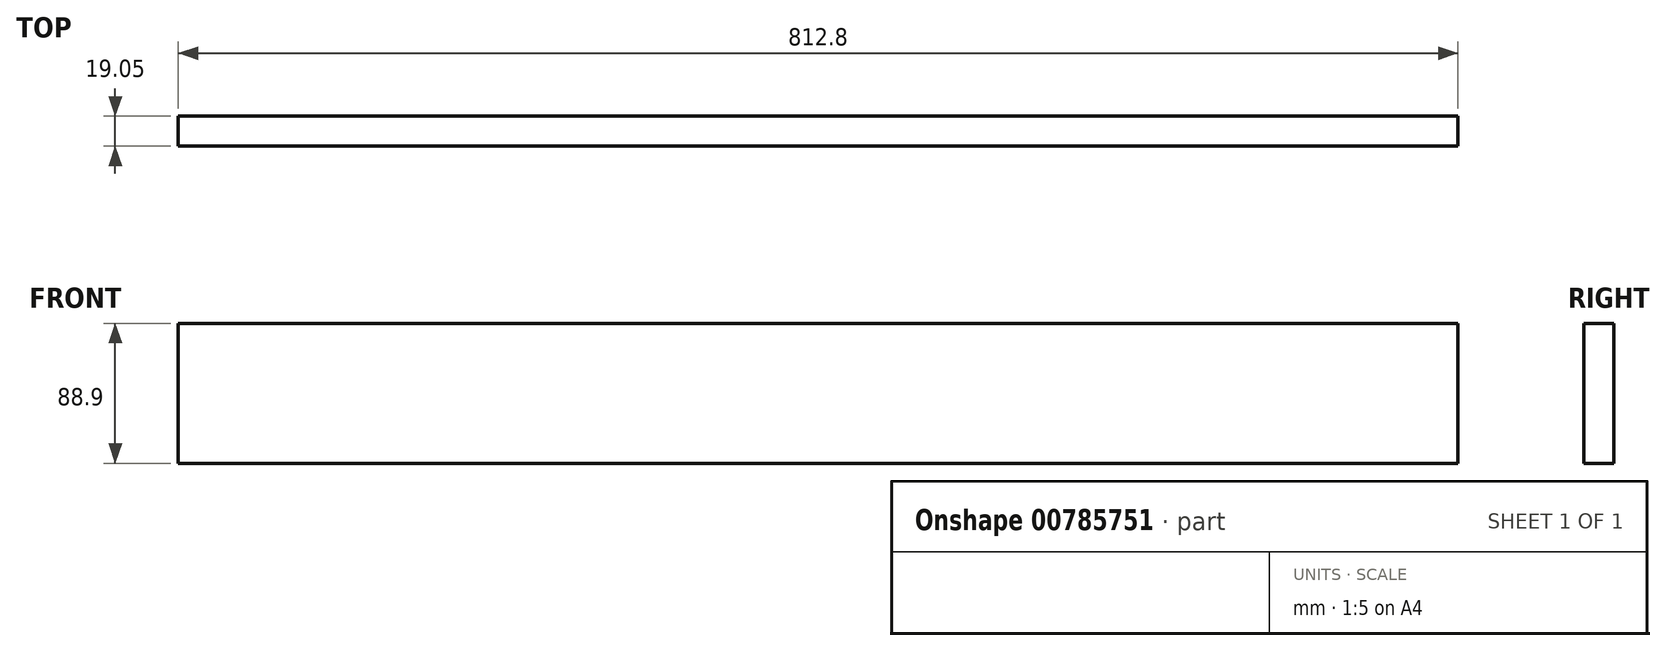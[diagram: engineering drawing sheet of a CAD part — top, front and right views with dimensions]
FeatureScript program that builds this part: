
annotation { "Feature Type Name" : "Feature", "Feature Type Description" : "" }
export const myFeature = defineFeature(function(context is Context, id is Id, definition is map)
    precondition{}
    {
        {
            var Q0;
            Q0=qCreatedBy(makeId("Top.planeOp"),FACE);
            var sketch = newSketch(context, id + "F0", { "sketchPlane" : qUnion([Q0])});
            skLineSegment(sketch, "E0.bottom", {"start": v(-47.4, 36.68) * mm, "end": v(765.4, 36.68) * mm});
            skLineSegment(sketch, "E0.top", {"start": v(-47.4, 17.63) * mm, "end": v(765.4, 17.63) * mm});
            skLineSegment(sketch, "E0.left", {"start": v(-47.4, 36.68) * mm, "end": v(-47.4, 17.63) * mm});
            skLineSegment(sketch, "E0.right", {"start": v(765.4, 36.68) * mm, "end": v(765.4, 17.63) * mm});
            skSolve(sketch);
        }
        {
            var Q0;
            Q0=makeQuery(id+"F0.imprint","IMPRINT",FACE,{"disambiguationData":[TD([[makeQuery(id+"F0.imprint","IMPRINT",EDGE,{"derivedFrom":sQuery(id+"F0.wireOp",EDGE,"E0.bottom")}),-1.0]])]});
            extrude(context, id + "F1", {"entities" : qUnion([Q0]), "oppositeDirection" : true, "depth" : 88.9 * mm, "offsetDistance" : 25.4 * mm});
        }
    });
